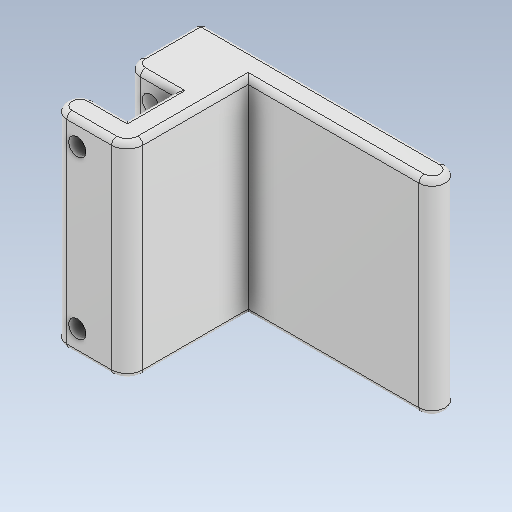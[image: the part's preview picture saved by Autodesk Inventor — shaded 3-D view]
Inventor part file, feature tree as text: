
AUTODESK INVENTOR PART (.ipt)
format: ipt  version: 2020.3 (Build 243373000, 373)  size: 224,768 bytes
history: native  units: mm
features: sketch x6, extrude x5, fillet x4, other x1, hole x1
ambient origin geometry x8: Origin, YZ Plane, XZ Plane, XY Plane, X Axis, Y Axis, Z Axis, Center Point
bodies: Body1 (feature_tree)
feature tree (17):
  other  "ソリッド1"
  extrude  "押し出し1"  Depth=5.0mm TaperAngle=0.0deg
  extrude  "押し出し2"  Depth=39.0mm
  extrude  "押し出し3"  Depth=49.0mm
  extrude  "押し出し4"  Depth=5.0mm
  extrude  "押し出し5"  Depth=39.0mm
  fillet  "フィレット1"  Radius=9.0mm
  fillet  "フィレット2"  Radius=9.0mm
  hole  "穴1"  [1 undecoded]
  fillet  "フィレット5"  Radius=9.0mm
  fillet  "フィレット6"  Radius=9.0mm
  sketch  "スケッチ1"
  sketch  "スケッチ2"
  sketch  "スケッチ3"
  sketch  "スケッチ4"
  sketch  "スケッチ5"
  sketch  "スケッチ6"
note: 1 required parameter value undecoded (feature->parameter linkage not recoverable at this tier; creation-order binding heuristic only, values carry confidence <= 0.55)
